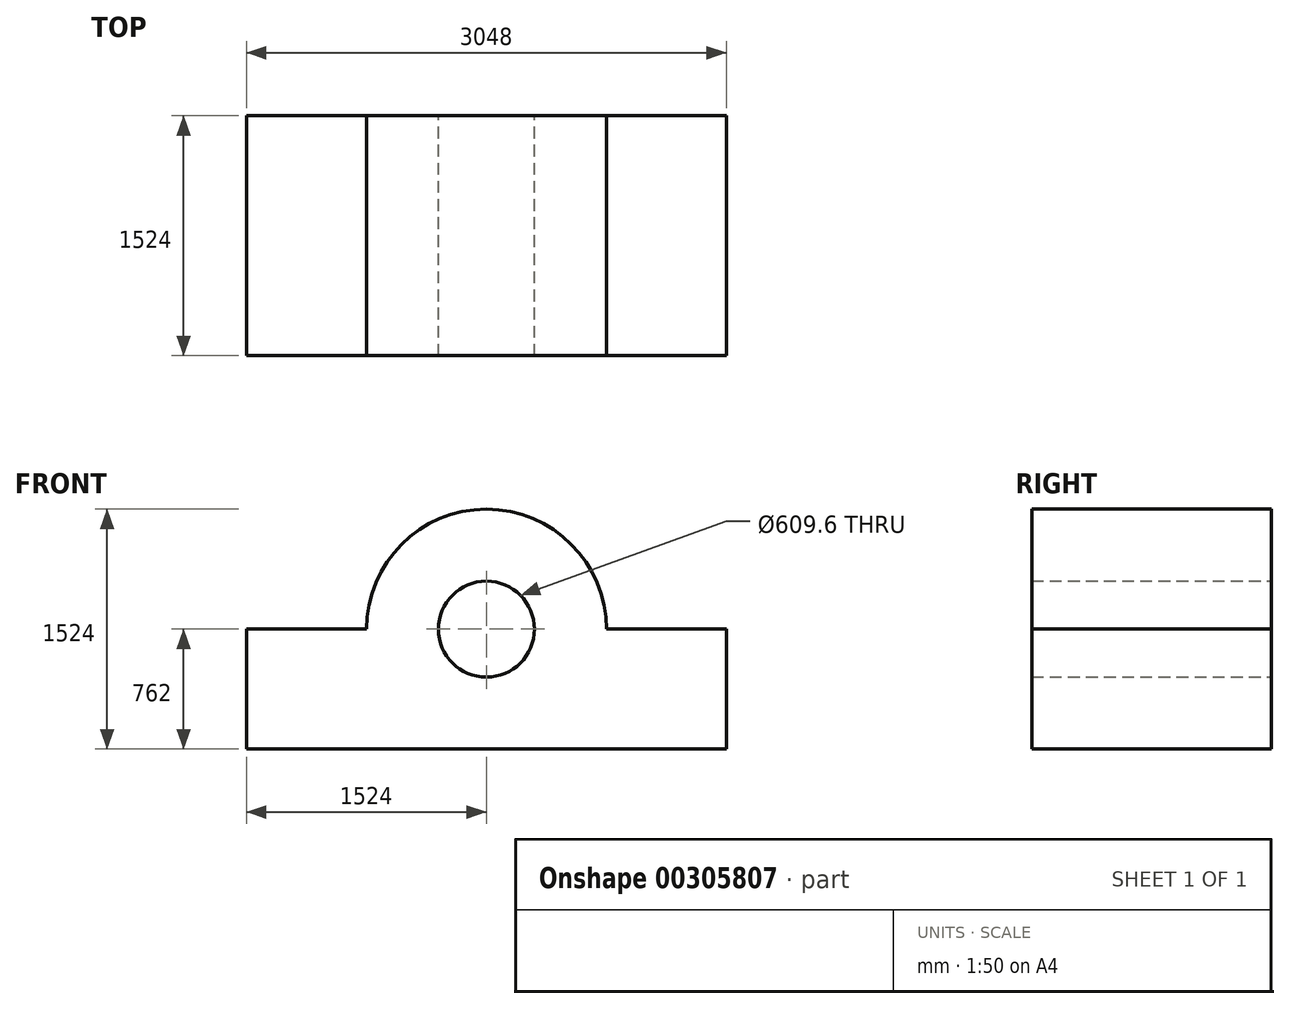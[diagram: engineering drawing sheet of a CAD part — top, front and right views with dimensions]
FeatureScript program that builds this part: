
annotation { "Feature Type Name" : "Feature", "Feature Type Description" : "" }
export const myFeature = defineFeature(function(context is Context, id is Id, definition is map)
    precondition{}
    {
        {
            var Q0;
            Q0=qCreatedBy(makeId("Front.planeOp"),FACE);
            var sketch = newSketch(context, id + "F0", { "sketchPlane" : qUnion([Q0])});
            skCircle(sketch, "E0", {"center": v(0, 0) * mm, "radius": 304.8 * mm});
            skArc(sketch, "E1", {"start": v(762, 0) * mm, "mid": v(0, 762) * mm, "end": v(-762, 0) * mm});
            skLineSegment(sketch, "E2", {"start": v(0, 0) * mm, "end": v(304.8, 0) * mm});
            skLineSegment(sketch, "E3", {"start": v(1524, 0) * mm, "end": v(1524, -762) * mm});
            skLineSegment(sketch, "E4", {"start": v(1524, -762) * mm, "end": v(-1524, -762) * mm});
            skLineSegment(sketch, "E5", {"start": v(-1524, -762) * mm, "end": v(-1524, 0) * mm});
            skLineSegment(sketch, "E6", {"start": v(-1524, 0) * mm, "end": v(-762, 0) * mm});
            skLineSegment(sketch, "E7.trimOffspring", {"start": v(-304.8, 0) * mm, "end": v(0, 0) * mm});
            skLineSegment(sketch, "E8.trimOffspring", {"start": v(762, 0) * mm, "end": v(1524, 0) * mm});
            skSolve(sketch);
        }
        {
            var Q0;
            Q0 = qSketchRegion(id + "F0", true);
            extrude(context, id + "F1", {"entities" : qUnion([Q0]), "depth" : 1524 * mm});
        }
    });
